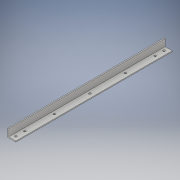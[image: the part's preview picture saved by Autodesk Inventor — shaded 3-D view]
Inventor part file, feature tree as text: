
AUTODESK INVENTOR PART (.ipt)
format: ipt  version: 2017 (Build 210142000, 142)  size: 137,728 bytes
history: native  units: in
note: dims shown in document units (in); Inventor stores cm internally (conversion verified against a paired STEP export)
features: hole x4, sketch x4, extrude x1
ambient origin geometry x8: Origin, YZ Plane, XZ Plane, XY Plane, X Axis, Y Axis, Z Axis, Center Point
bodies: Solid1 (feature_tree)
feature tree (9):
  extrude  "Extrusion1"  Depth=1.0in
  hole  "Hole1"  [1 undecoded]
  hole  "Hole5"  [1 undecoded]
  hole  "Hole6"  [1 undecoded]
  hole  "Hole7"  [1 undecoded]
  sketch  "Sketch2"  dims[d0=1.0in d1=1.0in]
  sketch  "Sketch8"  dims[d2=0.125in d3=19.375in d4=0.0in]
  sketch  "Sketch9"  dims[d5=0.5in d6=0.5in]
  sketch  "Sketch10"  dims[d7=0.7874in d9=18.375in d10=0.3937in d12=1.0in d14=0.266in d15=0.75in d16=0.385in d17=0.25in d18=0.5635in d19=1.0in d20=0.8108in d31=0.5in d59=0.5in d60=1.6in d61=0.266in d62=0.75in d63=0.507in d64=0.25in d65=0.5635in d66=1.0in d67=0.8108in d68=0.5in d69=1.6in d70=0.266in d71=0.75in d72=0.507in d73=0.25in d74=0.5635in d75=1.0in d76=0.8108in d77=0.5in d78=5.3in d79=1.1811in d81=4.4in d82=0.3937in d84=1.0in d86=0.266in d87=0.75in d88=0.507in d89=0.25in d90=0.5635in d91=1.0in d92=0.8108in]
note: 4 required parameter values undecoded (feature->parameter linkage not recoverable at this tier; creation-order binding heuristic only, values carry confidence <= 0.55)
